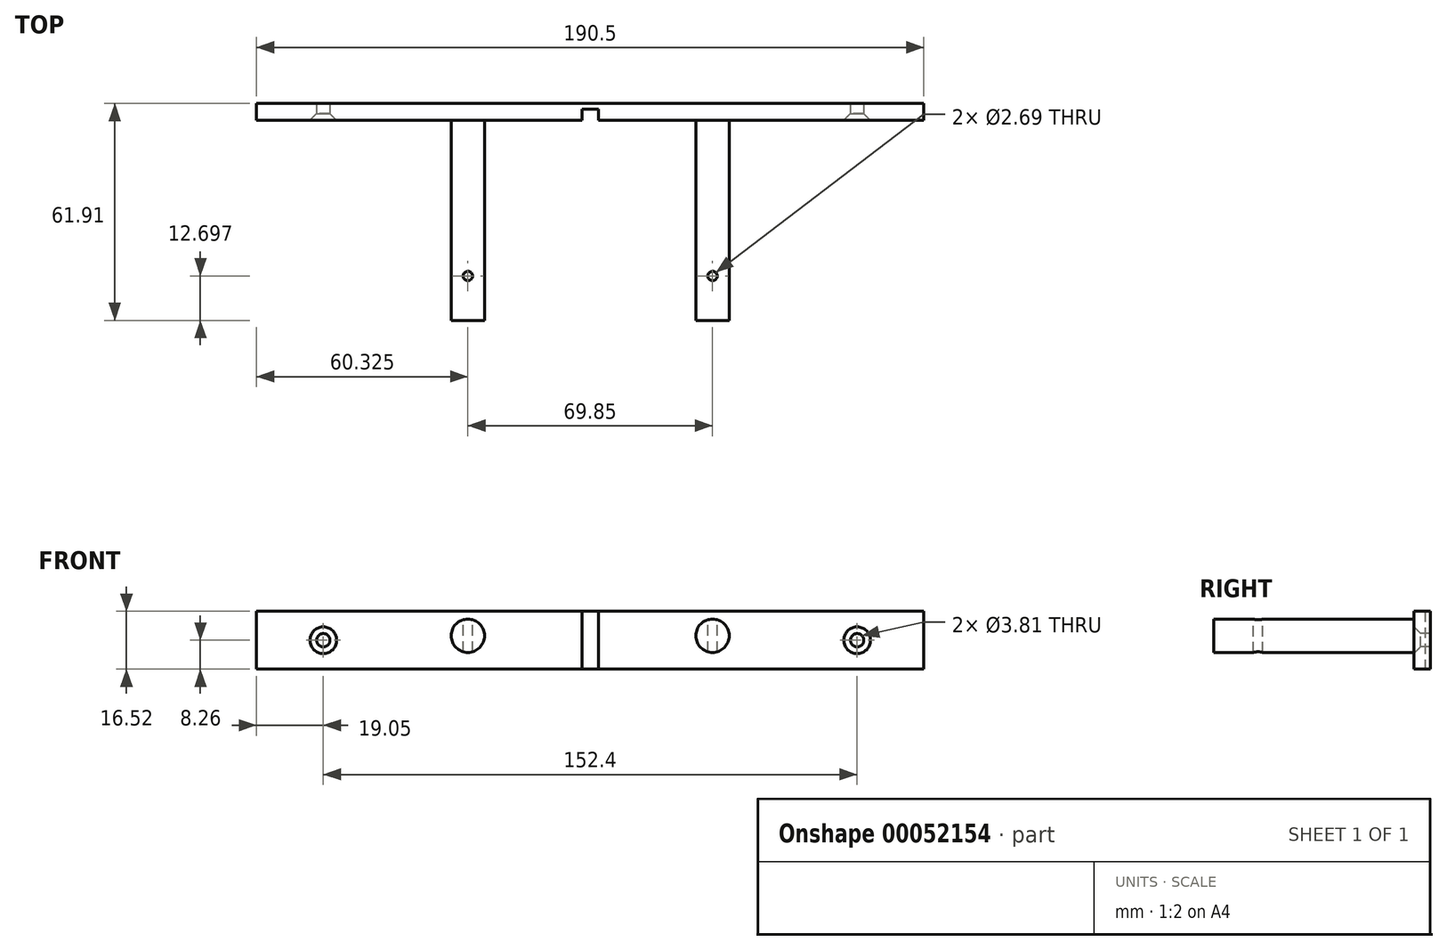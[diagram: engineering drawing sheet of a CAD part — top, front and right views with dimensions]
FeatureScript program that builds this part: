
annotation { "Feature Type Name" : "Feature", "Feature Type Description" : "" }
export const myFeature = defineFeature(function(context is Context, id is Id, definition is map)
    precondition{}
    {
        {
            var Q0;
            Q0=qCreatedBy(makeId("Front.planeOp"),FACE);
            var sketch = newSketch(context, id + "F0", { "sketchPlane" : qUnion([Q0])});
            skLineSegment(sketch, "E0.rect.bottom", {"start": v(95.25, 8.26) * mm, "end": v(-95.25, 8.26) * mm});
            skLineSegment(sketch, "E0.rect.top", {"start": v(95.25, -8.26) * mm, "end": v(-95.25, -8.26) * mm});
            skLineSegment(sketch, "E0.rect.left", {"start": v(95.25, 8.26) * mm, "end": v(95.25, -8.26) * mm});
            skLineSegment(sketch, "E0.rect.right", {"start": v(-95.25, 8.26) * mm, "end": v(-95.25, -8.26) * mm});
            skPoint(sketch, "E0.rect.middle", {"position": v(0, 0) * mm});
            skSolve(sketch);
        }
        {
            var Q0;
            Q0 = qSketchRegion(id + "F0", true);
            extrude(context, id + "F1", {"entities" : qUnion([Q0]), "depth" : 4.76 * mm});
        }
        {
            var Q0;
            Q0=makeQuery(id+"F1.opExtrude","CAP_FACE",FACE,{"disambiguationData":[OSD([sQuery(id+"F0.wireOp",EDGE,"E0.rect.bottom"),sQuery(id+"F0.wireOp",EDGE,"E0.rect.top"),sQuery(id+"F0.wireOp",EDGE,"E0.rect.left"),sQuery(id+"F0.wireOp",EDGE,"E0.rect.right")])],"isStart":false});
            var sketch = newSketch(context, id + "F2", { "sketchPlane" : qUnion([Q0])});
            skCircle(sketch, "E1", {"center": v(-34.93, 1.27) * mm, "radius": 4.76 * mm});
            skCircle(sketch, "E2", {"center": v(34.93, 1.27) * mm, "radius": 4.76 * mm});
            skSolve(sketch);
        }
        {
            var Q0;
            Q0 = qSketchRegion(id + "F2", true);
            extrude(context, id + "F3", {"entities" : qUnion([Q0]), "operationType" : NewBodyOperationType.ADD, "depth" : 57.15 * mm});
        }
        {
            var Q0;
            Q0=makeQuery(id+"F1.opExtrude","CAP_FACE",FACE,{"disambiguationData":[OSD([sQuery(id+"F0.wireOp",EDGE,"E0.rect.bottom"),sQuery(id+"F0.wireOp",EDGE,"E0.rect.top"),sQuery(id+"F0.wireOp",EDGE,"E0.rect.left"),sQuery(id+"F0.wireOp",EDGE,"E0.rect.right")])],"isStart":false});
            var sketch = newSketch(context, id + "F4", { "sketchPlane" : qUnion([Q0])});
            skPoint(sketch, "E3", {"position": v(-76.2, 0) * mm});
            skPoint(sketch, "E4", {"position": v(0, 0) * mm});
            skPoint(sketch, "E5", {"position": v(76.2, 0) * mm});
            skSolve(sketch);
        }
        {
            var Q0;
            Q0=sQuery(id+"F4.wireOp",VERTEX,"E3");
            var Q1;
            Q1=sQuery(id+"F4.wireOp",VERTEX,"E5");
            var Q2;
            Q2=makeQuery(id+"F1.opExtrude","SWEPT_BODY",BODY,{"disambiguationData":[OSD([sQuery(id+"F0.wireOp",EDGE,"E0.rect.bottom"),sQuery(id+"F0.wireOp",EDGE,"E0.rect.top"),sQuery(id+"F0.wireOp",EDGE,"E0.rect.left"),sQuery(id+"F0.wireOp",EDGE,"E0.rect.right")])]});
            hole(context, id + "F5", {"style" : HoleStyle.C_SINK, "holeDiameter" : 3.8 * mm, "cSinkDiameter" : 7.62 * mm, "endStyle" : HoleEndStyle.THROUGH, "locations" : qUnion([Q0, Q1]), "scope" : qUnion([Q2]), "cSinkAngle" : 90 * degree});
        }
        {
            var Q0;
            Q0=makeQuery(id+"F1.opExtrude","CAP_FACE",FACE,{"disambiguationData":[OSD([sQuery(id+"F0.wireOp",EDGE,"E0.rect.bottom"),sQuery(id+"F0.wireOp",EDGE,"E0.rect.top"),sQuery(id+"F0.wireOp",EDGE,"E0.rect.left"),sQuery(id+"F0.wireOp",EDGE,"E0.rect.right")])],"isStart":false});
            var sketch = newSketch(context, id + "F6", { "sketchPlane" : qUnion([Q0])});
            skLineSegment(sketch, "E6.rect.bottom", {"start": v(2.38, 8.26) * mm, "end": v(-2.38, 8.26) * mm});
            skLineSegment(sketch, "E6.rect.top", {"start": v(2.38, -8.26) * mm, "end": v(-2.38, -8.26) * mm});
            skLineSegment(sketch, "E6.rect.left", {"start": v(2.38, 8.26) * mm, "end": v(2.38, -8.26) * mm});
            skLineSegment(sketch, "E6.rect.right", {"start": v(-2.38, 8.26) * mm, "end": v(-2.38, -8.26) * mm});
            skPoint(sketch, "E6.rect.middle", {"position": v(0, 0) * mm});
            skSolve(sketch);
        }
        {
            var Q0;
            Q0 = qSketchRegion(id + "F6", true);
            extrude(context, id + "F7", {"entities" : qUnion([Q0]), "operationType" : NewBodyOperationType.REMOVE, "oppositeDirection" : true, "depth" : 3.17 * mm});
        }
        {
            var Q0;
            Q0=makeQuery(id+"F1.opExtrude","SWEPT_FACE",FACE,{"disambiguationData":[OSD([sQuery(id+"F0.wireOp",EDGE,"E0.rect.bottom")])]});
            var sketch = newSketch(context, id + "F8", { "sketchPlane" : qUnion([Q0])});
            skPoint(sketch, "E7", {"position": v(-34.93, -49.21) * mm});
            skPoint(sketch, "E8", {"position": v(34.93, -49.21) * mm});
            skCircle(sketch, "E9", {"center": v(-34.93, -49.21) * mm, "radius": 1.35 * mm});
            skCircle(sketch, "E10", {"center": v(34.93, -49.21) * mm, "radius": 1.35 * mm});
            skSolve(sketch);
        }
        {
            var Q0;
            Q0 = qSketchRegion(id + "F8", true);
            extrude(context, id + "F9", {"entities" : qUnion([Q0]), "operationType" : NewBodyOperationType.REMOVE, "endBound" : BoundingType.THROUGH_ALL, "oppositeDirection" : true, "depth" : 25.4 * mm});
        }
    });
